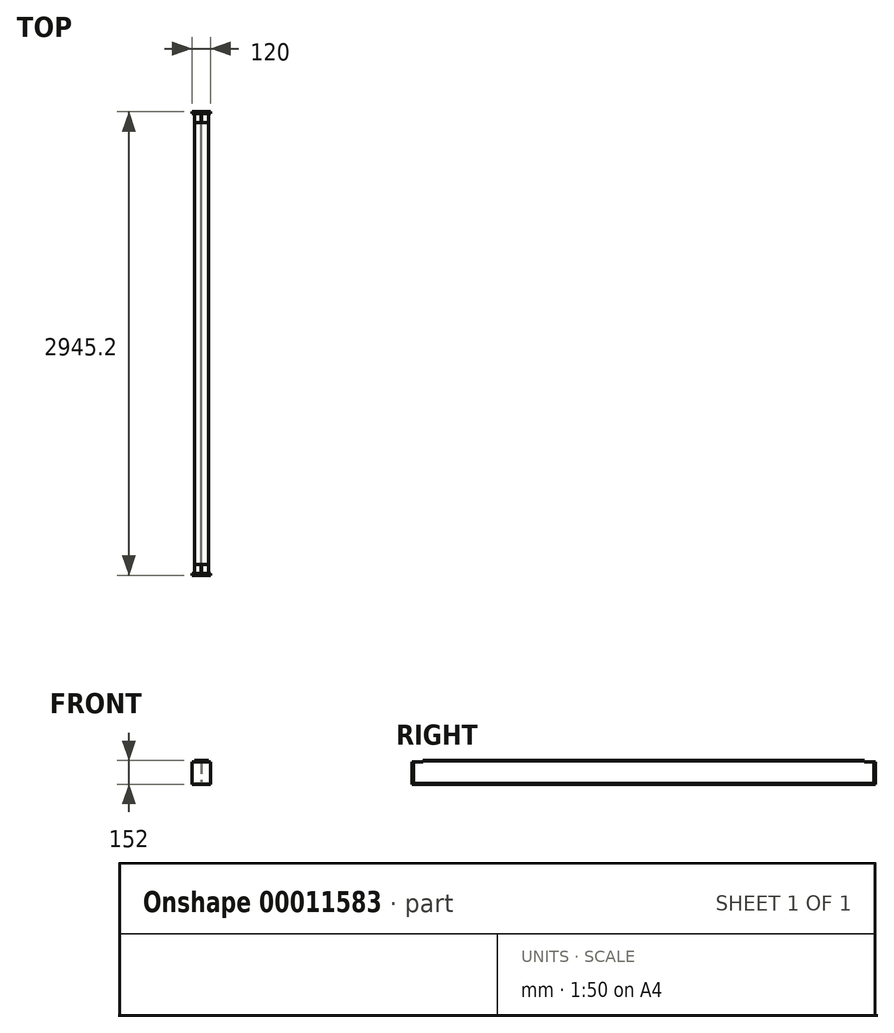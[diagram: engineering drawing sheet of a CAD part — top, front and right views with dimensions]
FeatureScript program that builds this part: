
annotation { "Feature Type Name" : "Feature", "Feature Type Description" : "" }
export const myFeature = defineFeature(function(context is Context, id is Id, definition is map)
    precondition{}
    {
        {
            var Q0;
            Q0=qCreatedBy(makeId("Front.planeOp"),FACE);
            var sketch = newSketch(context, id + "F0", { "sketchPlane" : qUnion([Q0])});
            skLineSegment(sketch, "E0.rect.bottom", {"start": v(44.5, 76) * mm, "end": v(-44.5, 76) * mm});
            skLineSegment(sketch, "E0.rect.top", {"start": v(44.5, -76) * mm, "end": v(-44.5, -76) * mm});
            skLineSegment(sketch, "E0.rect.left", {"start": v(44.5, 76) * mm, "end": v(44.5, 71.5) * mm});
            skLineSegment(sketch, "E0.rect.right", {"start": v(-44.5, 76) * mm, "end": v(-44.5, 71.5) * mm});
            skPoint(sketch, "E0.rect.middle", {"position": v(0, 0) * mm});
            skLineSegment(sketch, "E1.0", {"start": v(44.5, 71.5) * mm, "end": v(8.25, 71.5) * mm});
            skLineSegment(sketch, "E2.0", {"start": v(44.5, -71.5) * mm, "end": v(8.25, -71.5) * mm});
            skLineSegment(sketch, "E3", {"start": v(0, 71.5) * mm, "end": v(0, -71.5) * mm, "construction": true});
            skLineSegment(sketch, "E4.0", {"start": v(2.25, 65.5) * mm, "end": v(2.25, -65.5) * mm});
            skLineSegment(sketch, "E5.0", {"start": v(-2.25, 65.5) * mm, "end": v(-2.25, -65.5) * mm});
            skLineSegment(sketch, "E6.trimOffspring", {"start": v(-8.25, 71.5) * mm, "end": v(-44.5, 71.5) * mm});
            skLineSegment(sketch, "E7.trimOffspring", {"start": v(-8.25, -71.5) * mm, "end": v(-44.5, -71.5) * mm});
            skLineSegment(sketch, "E8.trimOffspring", {"start": v(44.5, -71.5) * mm, "end": v(44.5, -76) * mm});
            skLineSegment(sketch, "E9.trimOffspring", {"start": v(-44.5, -71.5) * mm, "end": v(-44.5, -76) * mm});
            skPoint(sketch, "E10.visualSharp", {"position": v(-2.25, -71.5) * mm});
            skArc(sketch, "E10.filletArc", {"start": v(-8.25, -71.5) * mm, "mid": v(-4, -69.74) * mm, "end": v(-2.25, -65.5) * mm});
            skPoint(sketch, "E11.visualSharp", {"position": v(2.25, -71.5) * mm});
            skArc(sketch, "E11.filletArc", {"start": v(2.25, -65.5) * mm, "mid": v(4, -69.74) * mm, "end": v(8.25, -71.5) * mm});
            skPoint(sketch, "E12.visualSharp", {"position": v(-2.25, 71.5) * mm});
            skArc(sketch, "E12.filletArc", {"start": v(-2.25, 65.5) * mm, "mid": v(-4, 69.74) * mm, "end": v(-8.25, 71.5) * mm});
            skPoint(sketch, "E13.visualSharp", {"position": v(2.25, 71.5) * mm});
            skArc(sketch, "E13.filletArc", {"start": v(8.25, 71.5) * mm, "mid": v(4, 69.74) * mm, "end": v(2.25, 65.5) * mm});
            skSolve(sketch);
        }
        {
            var Q0;
            Q0 = qSketchRegion(id + "F0", true);
            extrude(context, id + "F1", {"entities" : qUnion([Q0]), "depth" : 2945.2 * mm});
        }
        {
            var Q0;
            Q0=makeQuery(id+"F1.opExtrude","CAP_FACE",FACE,{"disambiguationData":[OSD([sQuery(id+"F0.wireOp",EDGE,"E0.rect.bottom"),sQuery(id+"F0.wireOp",EDGE,"E0.rect.top"),sQuery(id+"F0.wireOp",EDGE,"E0.rect.left"),sQuery(id+"F0.wireOp",EDGE,"E0.rect.right"),sQuery(id+"F0.wireOp",EDGE,"E1.0"),sQuery(id+"F0.wireOp",EDGE,"E2.0"),sQuery(id+"F0.wireOp",EDGE,"E4.0"),sQuery(id+"F0.wireOp",EDGE,"E5.0"),sQuery(id+"F0.wireOp",EDGE,"E6.trimOffspring"),sQuery(id+"F0.wireOp",EDGE,"E7.trimOffspring"),sQuery(id+"F0.wireOp",EDGE,"E8.trimOffspring"),sQuery(id+"F0.wireOp",EDGE,"E9.trimOffspring"),sQuery(id+"F0.wireOp",EDGE,"E10.filletArc"),sQuery(id+"F0.wireOp",EDGE,"E11.filletArc"),sQuery(id+"F0.wireOp",EDGE,"E12.filletArc"),sQuery(id+"F0.wireOp",EDGE,"E13.filletArc")])],"isStart":true});
            var sketch = newSketch(context, id + "F2", { "sketchPlane" : qUnion([Q0])});
            skLineSegment(sketch, "E14.rect.bottom", {"start": v(-60, 76) * mm, "end": v(60, 76) * mm});
            skLineSegment(sketch, "E14.rect.top", {"start": v(-60, -76) * mm, "end": v(60, -76) * mm});
            skLineSegment(sketch, "E14.rect.left", {"start": v(-60, 76) * mm, "end": v(-60, -76) * mm});
            skLineSegment(sketch, "E14.rect.right", {"start": v(60, 76) * mm, "end": v(60, -76) * mm});
            skPoint(sketch, "E14.rect.middle", {"position": v(0, 0) * mm});
            skSolve(sketch);
        }
        {
            var Q0;
            Q0 = qSketchRegion(id + "F2", true);
            extrude(context, id + "F3", {"entities" : qUnion([Q0]), "operationType" : NewBodyOperationType.ADD, "oppositeDirection" : true, "depth" : 11.05 * mm});
        }
        {
            var Q0;
            Q0=makeQuery(id+"F1.opExtrude","CAP_FACE",FACE,{"disambiguationData":[OSD([sQuery(id+"F0.wireOp",EDGE,"E0.rect.bottom"),sQuery(id+"F0.wireOp",EDGE,"E0.rect.top"),sQuery(id+"F0.wireOp",EDGE,"E0.rect.left"),sQuery(id+"F0.wireOp",EDGE,"E0.rect.right"),sQuery(id+"F0.wireOp",EDGE,"E1.0"),sQuery(id+"F0.wireOp",EDGE,"E2.0"),sQuery(id+"F0.wireOp",EDGE,"E4.0"),sQuery(id+"F0.wireOp",EDGE,"E5.0"),sQuery(id+"F0.wireOp",EDGE,"E6.trimOffspring"),sQuery(id+"F0.wireOp",EDGE,"E7.trimOffspring"),sQuery(id+"F0.wireOp",EDGE,"E8.trimOffspring"),sQuery(id+"F0.wireOp",EDGE,"E9.trimOffspring"),sQuery(id+"F0.wireOp",EDGE,"E10.filletArc"),sQuery(id+"F0.wireOp",EDGE,"E11.filletArc"),sQuery(id+"F0.wireOp",EDGE,"E12.filletArc"),sQuery(id+"F0.wireOp",EDGE,"E13.filletArc")])],"isStart":false});
            var sketch = newSketch(context, id + "F4", { "sketchPlane" : qUnion([Q0])});
            skLineSegment(sketch, "E15.rect.bottom", {"start": v(60, 76) * mm, "end": v(-60, 76) * mm});
            skLineSegment(sketch, "E15.rect.top", {"start": v(60, -76) * mm, "end": v(-60, -76) * mm});
            skLineSegment(sketch, "E15.rect.left", {"start": v(60, 76) * mm, "end": v(60, -76) * mm});
            skLineSegment(sketch, "E15.rect.right", {"start": v(-60, 76) * mm, "end": v(-60, -76) * mm});
            skPoint(sketch, "E15.rect.middle", {"position": v(0, 0) * mm});
            skSolve(sketch);
        }
        {
            var Q0;
            Q0 = qSketchRegion(id + "F4", true);
            extrude(context, id + "F5", {"entities" : qUnion([Q0]), "operationType" : NewBodyOperationType.ADD, "oppositeDirection" : true, "depth" : 11.05 * mm});
        }
        {
            var Q0;
            Q0=makeQuery(id+"F5.boolean.opBoolean","MERGE",FACE,{"derivedFrom":[makeQuery(id+"F1.opExtrude","CAP_FACE",FACE,{"disambiguationData":[OSD([sQuery(id+"F0.wireOp",EDGE,"E0.rect.bottom"),sQuery(id+"F0.wireOp",EDGE,"E0.rect.top"),sQuery(id+"F0.wireOp",EDGE,"E0.rect.left"),sQuery(id+"F0.wireOp",EDGE,"E0.rect.right"),sQuery(id+"F0.wireOp",EDGE,"E1.0"),sQuery(id+"F0.wireOp",EDGE,"E2.0"),sQuery(id+"F0.wireOp",EDGE,"E4.0"),sQuery(id+"F0.wireOp",EDGE,"E5.0"),sQuery(id+"F0.wireOp",EDGE,"E6.trimOffspring"),sQuery(id+"F0.wireOp",EDGE,"E7.trimOffspring"),sQuery(id+"F0.wireOp",EDGE,"E8.trimOffspring"),sQuery(id+"F0.wireOp",EDGE,"E9.trimOffspring"),sQuery(id+"F0.wireOp",EDGE,"E10.filletArc"),sQuery(id+"F0.wireOp",EDGE,"E11.filletArc"),sQuery(id+"F0.wireOp",EDGE,"E12.filletArc"),sQuery(id+"F0.wireOp",EDGE,"E13.filletArc")])],"isStart":false}),makeQuery(id+"F5.opExtrude","CAP_FACE",FACE,{"disambiguationData":[OSD([sQuery(id+"F4.wireOp",EDGE,"E15.rect.bottom"),sQuery(id+"F4.wireOp",EDGE,"E15.rect.top"),sQuery(id+"F4.wireOp",EDGE,"E15.rect.left"),sQuery(id+"F4.wireOp",EDGE,"E15.rect.right")])],"isStart":true})]});
            var sketch = newSketch(context, id + "F6", { "sketchPlane" : qUnion([Q0])});
            skLineSegment(sketch, "E16.bottom", {"start": v(-60, 76) * mm, "end": v(60, 76) * mm});
            skLineSegment(sketch, "E16.top", {"start": v(-60, 65.5) * mm, "end": v(60, 65.5) * mm});
            skLineSegment(sketch, "E16.left", {"start": v(-60, 76) * mm, "end": v(-60, 65.5) * mm});
            skLineSegment(sketch, "E16.right", {"start": v(60, 76) * mm, "end": v(60, 65.5) * mm});
            skSolve(sketch);
        }
        {
            var Q0;
            Q0 = qSketchRegion(id + "F6", true);
            extrude(context, id + "F7", {"entities" : qUnion([Q0]), "operationType" : NewBodyOperationType.REMOVE, "oppositeDirection" : true, "depth" : 70.5 * mm});
        }
        {
            var Q0;
            Q0=makeQuery(id+"F3.boolean.opBoolean","MERGE",FACE,{"derivedFrom":[makeQuery(id+"F1.opExtrude","CAP_FACE",FACE,{"disambiguationData":[OSD([sQuery(id+"F0.wireOp",EDGE,"E0.rect.bottom"),sQuery(id+"F0.wireOp",EDGE,"E0.rect.top"),sQuery(id+"F0.wireOp",EDGE,"E0.rect.left"),sQuery(id+"F0.wireOp",EDGE,"E0.rect.right"),sQuery(id+"F0.wireOp",EDGE,"E1.0"),sQuery(id+"F0.wireOp",EDGE,"E2.0"),sQuery(id+"F0.wireOp",EDGE,"E4.0"),sQuery(id+"F0.wireOp",EDGE,"E5.0"),sQuery(id+"F0.wireOp",EDGE,"E6.trimOffspring"),sQuery(id+"F0.wireOp",EDGE,"E7.trimOffspring"),sQuery(id+"F0.wireOp",EDGE,"E8.trimOffspring"),sQuery(id+"F0.wireOp",EDGE,"E9.trimOffspring"),sQuery(id+"F0.wireOp",EDGE,"E10.filletArc"),sQuery(id+"F0.wireOp",EDGE,"E11.filletArc"),sQuery(id+"F0.wireOp",EDGE,"E12.filletArc"),sQuery(id+"F0.wireOp",EDGE,"E13.filletArc")])],"isStart":true}),makeQuery(id+"F3.opExtrude","CAP_FACE",FACE,{"disambiguationData":[OSD([sQuery(id+"F2.wireOp",EDGE,"E14.rect.bottom"),sQuery(id+"F2.wireOp",EDGE,"E14.rect.top"),sQuery(id+"F2.wireOp",EDGE,"E14.rect.left"),sQuery(id+"F2.wireOp",EDGE,"E14.rect.right")])],"isStart":true})]});
            var sketch = newSketch(context, id + "F8", { "sketchPlane" : qUnion([Q0])});
            skLineSegment(sketch, "E17.bottom", {"start": v(-60, 76) * mm, "end": v(60, 76) * mm});
            skLineSegment(sketch, "E17.top", {"start": v(-60, 65.5) * mm, "end": v(60, 65.5) * mm});
            skLineSegment(sketch, "E17.left", {"start": v(-60, 76) * mm, "end": v(-60, 65.5) * mm});
            skLineSegment(sketch, "E17.right", {"start": v(60, 76) * mm, "end": v(60, 65.5) * mm});
            skSolve(sketch);
        }
        {
            var Q0;
            Q0 = qSketchRegion(id + "F8", true);
            extrude(context, id + "F9", {"entities" : qUnion([Q0]), "operationType" : NewBodyOperationType.REMOVE, "oppositeDirection" : true, "depth" : 70.5 * mm});
        }
    });
